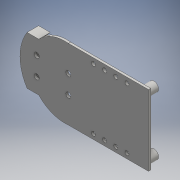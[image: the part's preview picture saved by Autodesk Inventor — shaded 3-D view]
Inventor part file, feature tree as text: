
AUTODESK INVENTOR PART (.ipt)
format: ipt  version: 2016 (Build 200138000, 138)  size: 186,368 bytes
history: native  units: mm
features: sketch x5, hole x3, extrude x2, projected_geometry x1
ambient origin geometry x8: Origin, YZ Plane, XZ Plane, XY Plane, X Axis, Y Axis, Z Axis, Center Point
bodies: Solid1 (feature_tree)
feature tree (11):
  extrude  "Extrusion1"  Depth=76.0mm
  extrude  "Extrusion2"  Depth=10.0mm
  hole  "Hole1"  [1 undecoded]
  hole  "Hole2"  [1 undecoded]
  hole  "Hole3"  [1 undecoded]
  sketch  "Sketch1"  dims[d1=86.0mm d2=76.0mm]
  sketch  "Sketch2"  dims[d3=10.0mm d4=10.0mm]
  sketch  "Sketch4"  dims[d6=12.0mm d7=12.0mm]
  sketch  "Sketch5"  dims[d8=2.4mm d9=0.0mm d10=10.0mm]
  projected_geometry  "Projected Loop1"
  sketch  "Sketch6"  dims[d11=10.0mm d12=63.0mm d13=6.5mm d14=6.5mm d15=6.5mm d16=10.0mm d17=0.0mm d20=6.5mm d21=6.5mm d22=127.167mm d23=6.5mm d24=6.5mm d25=6.0mm d26=4.0mm d27=2.0mm d28=90.0deg d29=9.0mm d30=0.0mm d36=5.5mm d38=5.5mm d39=10.0mm d40=10.0mm d41=5.5mm d42=5.5mm d43=34.0mm d44=34.0mm d45=5.5mm d46=6.0mm d47=4.0mm d48=2.0mm d49=90.0deg d50=9.0mm d51=0.0mm d52=27.0mm d53=27.0mm d54=4.4mm d55=23.0mm d56=5.5mm d57=4.4mm d58=12.0mm d59=4.4mm d60=12.0mm d61=4.4mm d62=12.0mm d63=4.4mm d64=6.0mm d65=4.0mm d66=2.0mm d67=90.0deg d68=9.0mm d69=0.0mm d70=63.0mm]
note: 3 required parameter values undecoded (feature->parameter linkage not recoverable at this tier; creation-order binding heuristic only, values carry confidence <= 0.55)
